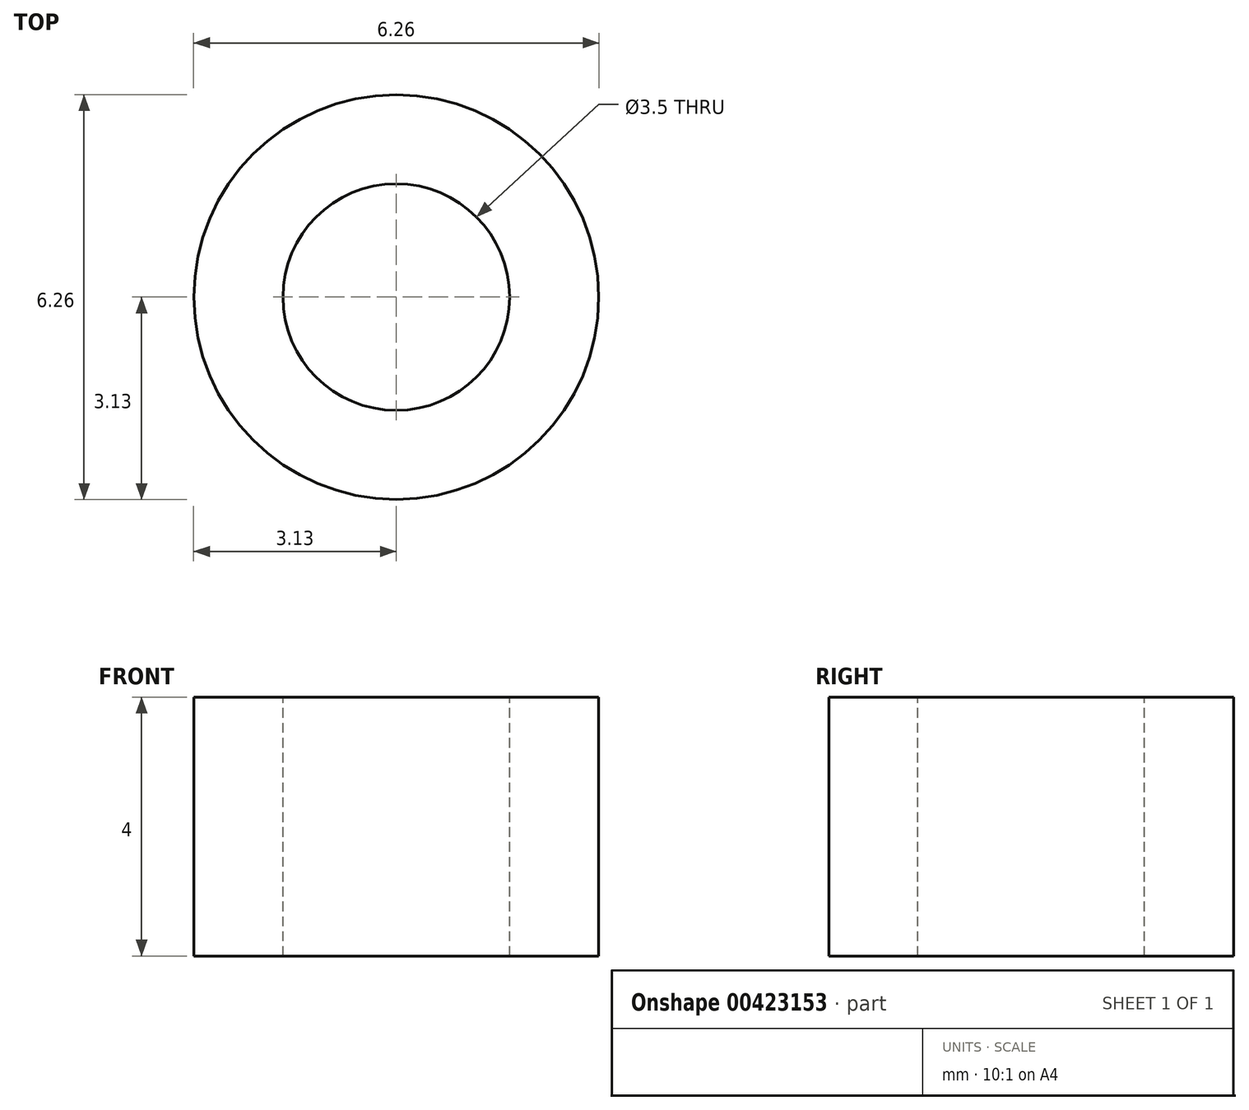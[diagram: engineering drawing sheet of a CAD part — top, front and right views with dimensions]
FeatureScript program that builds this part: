
annotation { "Feature Type Name" : "Feature", "Feature Type Description" : "" }
export const myFeature = defineFeature(function(context is Context, id is Id, definition is map)
    precondition{}
    {
        {
            assignVariable(context, id + "F0", {"name" : "spacer_height", "anyValue" : 4});
        }
        {
            assignVariable(context, id + "F1", {"name" : "spacer_hole", "anyValue" : 3.5});
        }
        {
            var Q0;
            Q0=qCreatedBy(makeId("Top.planeOp"),FACE);
            var sketch = newSketch(context, id + "F2", { "sketchPlane" : qUnion([Q0])});
            skCircle(sketch, "E0", {"center": v(0, 0) * mm, "radius": 3.12 * mm});
            skPoint(sketch, "E1", {"position": v(0.02, -0.05) * mm});
            skSolve(sketch);
        }
        {
            var Q0;
            Q0=makeQuery(id+"F2.imprint","IMPRINT",FACE,{"disambiguationData":[TD([[makeQuery(id+"F2.imprint","IMPRINT",EDGE,{"derivedFrom":sQuery(id+"F2.wireOp",EDGE,"E0")}),1.0]])]});
            extrude(context, id + "F3", {"entities" : qUnion([Q0]), "depth" : (getVariable(context, 'spacer_height')) * mm});
        }
        {
            var Q0;
            Q0=makeQuery(id+"F3.opExtrude","CAP_FACE",FACE,{"disambiguationData":[OSD([sQuery(id+"F2.wireOp",EDGE,"E0")])],"isStart":false});
            var sketch = newSketch(context, id + "F4", { "sketchPlane" : qUnion([Q0])});
            skPoint(sketch, "E2", {"position": v(0, 0) * mm});
            skSolve(sketch);
        }
        {
            var Q0;
            Q0=sQuery(id+"F4.wireOp",VERTEX,"E2");
            var Q1;
            Q1=makeQuery(id+"F3.opExtrude","SWEPT_BODY",BODY,{"disambiguationData":[OSD([sQuery(id+"F2.wireOp",EDGE,"E0")])]});
            hole(context, id + "F5", {"style" : HoleStyle.SIMPLE, "endStyle" : HoleEndStyle.THROUGH, "holeDiameter" : (getVariable(context, 'spacer_hole')) * mm, "isTappedThrough" : true, "tappedDepth" : 12.7 * mm, "tapClearance" : 3, "startFromSketch" : true, "locations" : qUnion([Q0]), "scope" : qUnion([Q1])});
        }
    });
